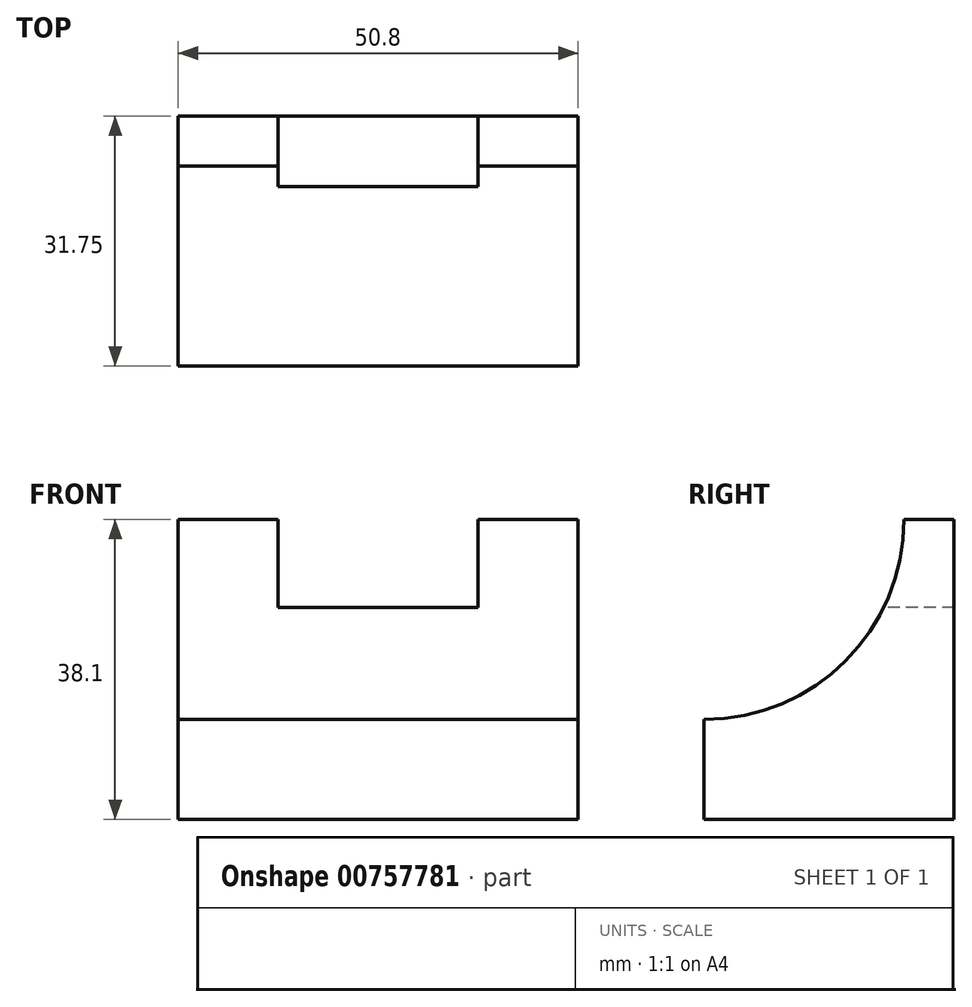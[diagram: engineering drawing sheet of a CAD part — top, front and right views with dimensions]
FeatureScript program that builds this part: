
annotation { "Feature Type Name" : "Feature", "Feature Type Description" : "" }
export const myFeature = defineFeature(function(context is Context, id is Id, definition is map)
    precondition{}
    {
        {
            var Q0;
            Q0=qCreatedBy(makeId("Front.planeOp"),FACE);
            var sketch = newSketch(context, id + "F0", { "sketchPlane" : qUnion([Q0])});
            skLineSegment(sketch, "E0", {"start": v(-25.66, 0) * mm, "end": v(25.14, 0) * mm});
            skLineSegment(sketch, "E1", {"start": v(25.14, 0) * mm, "end": v(25.14, 38.1) * mm});
            skLineSegment(sketch, "E2", {"start": v(25.14, 38.1) * mm, "end": v(-25.66, 38.1) * mm});
            skLineSegment(sketch, "E3", {"start": v(-25.66, 38.1) * mm, "end": v(-25.66, 0) * mm});
            skSolve(sketch);
        }
        {
            var Q0;
            Q0 = qSketchRegion(id + "F0", true);
            extrude(context, id + "F1", {"entities" : qUnion([Q0]), "depth" : 31.75 * mm, "offsetDistance" : 25.4 * mm});
        }
        {
            var Q0;
            Q0=makeQuery(id+"F1.opExtrude","SWEPT_FACE",FACE,{"disambiguationData":[OSD([sQuery(id+"F0.wireOp",EDGE,"E1")])]});
            var sketch = newSketch(context, id + "F2", { "sketchPlane" : qUnion([Q0])});
            skLineSegment(sketch, "E4", {"start": v(-6.35, 38.1) * mm, "end": v(-6.35, 0) * mm});
            skLineSegment(sketch, "E5", {"start": v(-31.75, 12.7) * mm, "end": v(0, 12.7) * mm});
            skArc(sketch, "E6", {"start": v(-31.75, 12.7) * mm, "mid": v(-13.79, 20.14) * mm, "end": v(-6.35, 38.1) * mm});
            skSolve(sketch);
        }
        {
            var Q0;
            {var subQ0=sQuery(id+"F2.wireOp",EDGE,"E6");Q0=makeQuery(id+"F2.imprint","IMPRINT",FACE,{"disambiguationData":[TD([[makeQuery(id+"F2.imprint","IMPRINT",EDGE,{"derivedFrom":subQ0}),1.0]])]});}
            extrude(context, id + "F3", {"entities" : qUnion([Q0]), "operationType" : NewBodyOperationType.REMOVE, "endBound" : BoundingType.THROUGH_ALL, "oppositeDirection" : true, "depth" : 25.4 * mm, "offsetDistance" : 25.4 * mm});
        }
        {
            var Q0;
            Q0=makeQuery(id+"F1.opExtrude","CAP_FACE",FACE,{"disambiguationData":[OSD([sQuery(id+"F0.wireOp",EDGE,"E0"),sQuery(id+"F0.wireOp",EDGE,"E1"),sQuery(id+"F0.wireOp",EDGE,"E2"),sQuery(id+"F0.wireOp",EDGE,"E3")])],"isStart":false});
            var sketch = newSketch(context, id + "F4", { "sketchPlane" : qUnion([Q0])});
            skLineSegment(sketch, "E7", {"start": v(0, 0) * mm, "end": v(25.14, 0) * mm});
            skLineSegment(sketch, "E8", {"start": v(25.14, 0) * mm, "end": v(25.14, 38.13) * mm});
            skLineSegment(sketch, "E9", {"start": v(25.14, 38.13) * mm, "end": v(-25.66, 38.13) * mm});
            skLineSegment(sketch, "E10", {"start": v(-25.66, 38.13) * mm, "end": v(-25.66, 0) * mm});
            skLineSegment(sketch, "E11", {"start": v(-25.66, 0) * mm, "end": v(25.14, 0) * mm});
            skLineSegment(sketch, "E12", {"start": v(-12.96, 38.13) * mm, "end": v(-12.96, 26.9) * mm});
            skLineSegment(sketch, "E13", {"start": v(-12.96, 26.9) * mm, "end": v(12.44, 26.9) * mm});
            skLineSegment(sketch, "E14", {"start": v(12.44, 26.9) * mm, "end": v(12.44, 38.13) * mm});
            skSolve(sketch);
        }
        {
            var Q0;
            {var subQ0=sQuery(id+"F4.wireOp",EDGE,"E12");Q0=makeQuery(id+"F4.imprint","IMPRINT",FACE,{"disambiguationData":[TD([[makeQuery(id+"F4.imprint","IMPRINT",EDGE,{"derivedFrom":subQ0}),1.0]])]});}
            extrude(context, id + "F5", {"entities" : qUnion([Q0]), "operationType" : NewBodyOperationType.REMOVE, "endBound" : BoundingType.THROUGH_ALL, "oppositeDirection" : true, "depth" : 25.4 * mm, "offsetDistance" : 25.4 * mm});
        }
    });
